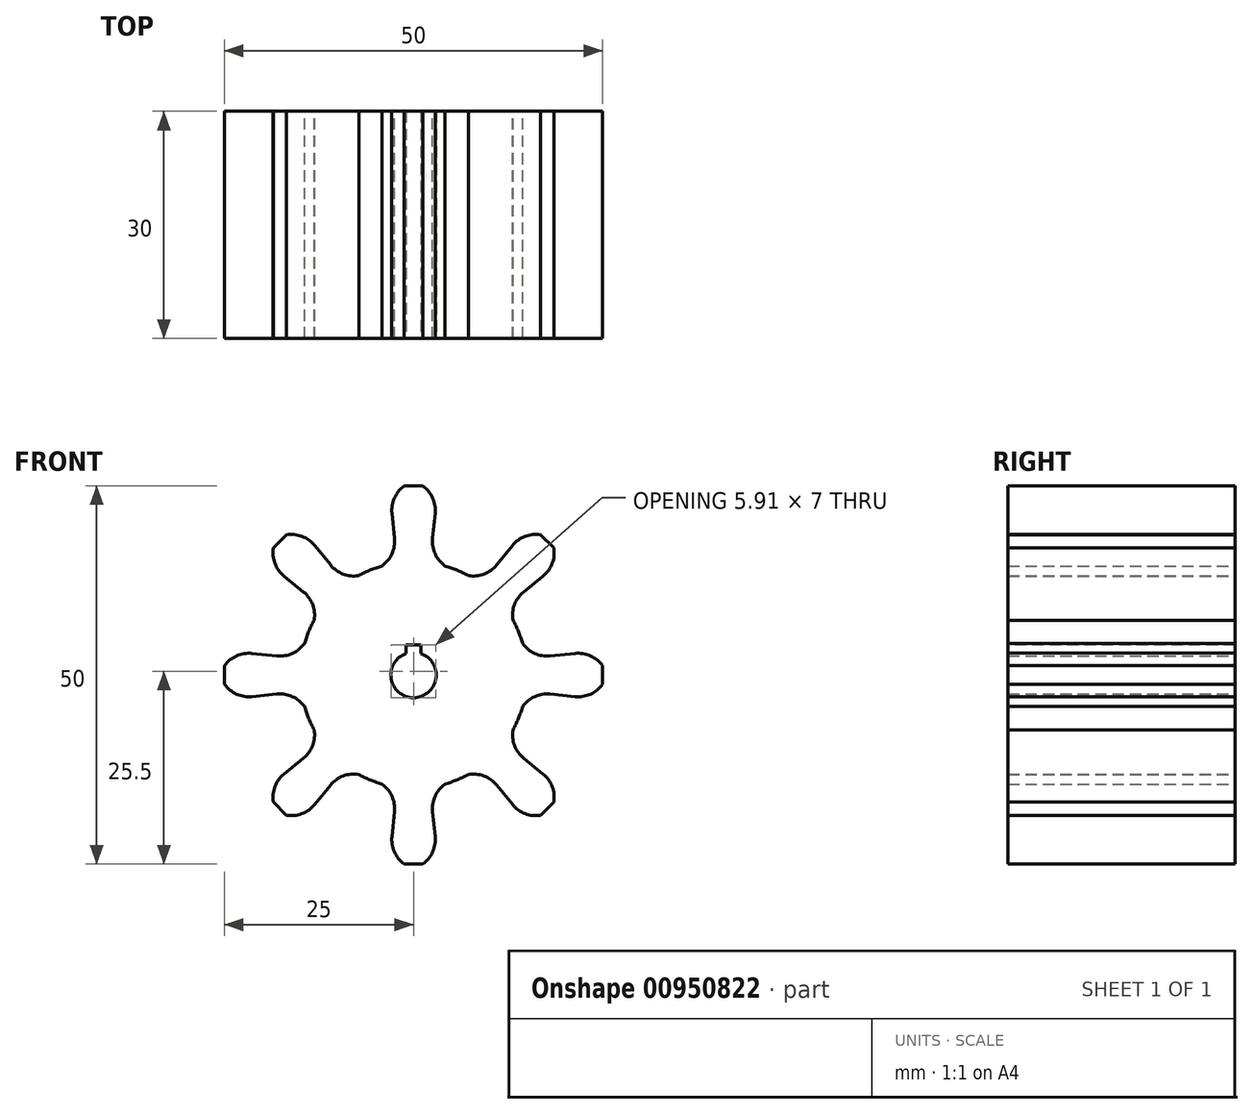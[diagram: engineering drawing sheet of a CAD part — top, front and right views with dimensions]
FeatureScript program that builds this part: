
annotation { "Feature Type Name" : "Feature", "Feature Type Description" : "" }
export const myFeature = defineFeature(function(context is Context, id is Id, definition is map)
    precondition{}
    {
        {
            var Q0;
            Q0=qCreatedBy(makeId("Front.planeOp"),FACE);
            var sketch = newSketch(context, id + "F0", { "sketchPlane" : qUnion([Q0])});
            skArc(sketch, "E0", {"start": v(-13.14, 7.24) * mm, "mid": v(-13.86, 5.74) * mm, "end": v(-14.4, 4.17) * mm});
            skArc(sketch, "E1", {"start": v(-4.17, 14.4) * mm, "mid": v(-2.86, 16.01) * mm, "end": v(-2.53, 18.06) * mm});
            skLineSegment(sketch, "E2", {"start": v(-2.53, 18.06) * mm, "end": v(-2.86, 21.35) * mm});
            skLineSegment(sketch, "E3", {"start": v(-1.22, 25) * mm, "end": v(1.22, 25) * mm});
            skArc(sketch, "E4", {"start": v(-1.22, 25) * mm, "mid": v(-2.53, 23.4) * mm, "end": v(-2.86, 21.35) * mm});
            skArc(sketch, "E5.MirrorCS", {"start": v(1.22, 25) * mm, "mid": v(2.53, 23.4) * mm, "end": v(2.86, 21.35) * mm});
            skLineSegment(sketch, "E6.MirrorCS", {"start": v(2.53, 18.06) * mm, "end": v(2.86, 21.35) * mm});
            skArc(sketch, "E7.MirrorCS", {"start": v(4.17, 14.4) * mm, "mid": v(2.86, 16.01) * mm, "end": v(2.53, 18.06) * mm});
            skLineSegment(sketch, "E8.1.0", {"start": v(-18.54, 16.81) * mm, "end": v(-16.81, 18.54) * mm});
            skArc(sketch, "E8.1.1", {"start": v(-18.54, 16.81) * mm, "mid": v(-18.33, 14.75) * mm, "end": v(-17.12, 13.07) * mm});
            skLineSegment(sketch, "E8.1.2", {"start": v(-14.56, 10.98) * mm, "end": v(-17.12, 13.07) * mm});
            skArc(sketch, "E8.1.3", {"start": v(-13.14, 7.24) * mm, "mid": v(-13.34, 9.3) * mm, "end": v(-14.56, 10.98) * mm});
            skArc(sketch, "E8.1.4", {"start": v(-7.24, 13.14) * mm, "mid": v(-9.3, 13.34) * mm, "end": v(-10.98, 14.56) * mm});
            skLineSegment(sketch, "E8.1.5", {"start": v(-10.98, 14.56) * mm, "end": v(-13.07, 17.12) * mm});
            skArc(sketch, "E8.1.6", {"start": v(-16.81, 18.54) * mm, "mid": v(-14.75, 18.33) * mm, "end": v(-13.07, 17.12) * mm});
            skLineSegment(sketch, "E8.2.0", {"start": v(-25, -1.22) * mm, "end": v(-25, 1.22) * mm});
            skArc(sketch, "E8.2.1", {"start": v(-25, -1.22) * mm, "mid": v(-23.4, -2.53) * mm, "end": v(-21.35, -2.86) * mm});
            skLineSegment(sketch, "E8.2.2", {"start": v(-18.06, -2.53) * mm, "end": v(-21.35, -2.86) * mm});
            skArc(sketch, "E8.2.3", {"start": v(-14.4, -4.17) * mm, "mid": v(-16.01, -2.86) * mm, "end": v(-18.06, -2.53) * mm});
            skArc(sketch, "E8.2.4", {"start": v(-14.4, 4.17) * mm, "mid": v(-16.01, 2.86) * mm, "end": v(-18.06, 2.53) * mm});
            skLineSegment(sketch, "E8.2.5", {"start": v(-18.06, 2.53) * mm, "end": v(-21.35, 2.86) * mm});
            skArc(sketch, "E8.2.6", {"start": v(-25, 1.22) * mm, "mid": v(-23.4, 2.53) * mm, "end": v(-21.35, 2.86) * mm});
            skLineSegment(sketch, "E8.3.0", {"start": v(-16.81, -18.54) * mm, "end": v(-18.54, -16.81) * mm});
            skArc(sketch, "E8.3.1", {"start": v(-16.81, -18.54) * mm, "mid": v(-14.75, -18.33) * mm, "end": v(-13.07, -17.12) * mm});
            skLineSegment(sketch, "E8.3.2", {"start": v(-10.98, -14.56) * mm, "end": v(-13.07, -17.12) * mm});
            skArc(sketch, "E8.3.3", {"start": v(-7.24, -13.14) * mm, "mid": v(-9.3, -13.34) * mm, "end": v(-10.98, -14.56) * mm});
            skArc(sketch, "E8.3.4", {"start": v(-13.14, -7.24) * mm, "mid": v(-13.34, -9.3) * mm, "end": v(-14.56, -10.98) * mm});
            skLineSegment(sketch, "E8.3.5", {"start": v(-14.56, -10.98) * mm, "end": v(-17.12, -13.07) * mm});
            skArc(sketch, "E8.3.6", {"start": v(-18.54, -16.81) * mm, "mid": v(-18.33, -14.75) * mm, "end": v(-17.12, -13.07) * mm});
            skLineSegment(sketch, "E8.4.0", {"start": v(1.22, -25) * mm, "end": v(-1.22, -25) * mm});
            skArc(sketch, "E8.4.1", {"start": v(1.22, -25) * mm, "mid": v(2.53, -23.4) * mm, "end": v(2.86, -21.35) * mm});
            skLineSegment(sketch, "E8.4.2", {"start": v(2.53, -18.06) * mm, "end": v(2.86, -21.35) * mm});
            skArc(sketch, "E8.4.3", {"start": v(4.17, -14.4) * mm, "mid": v(2.86, -16.01) * mm, "end": v(2.53, -18.06) * mm});
            skArc(sketch, "E8.4.4", {"start": v(-4.17, -14.4) * mm, "mid": v(-2.86, -16.01) * mm, "end": v(-2.53, -18.06) * mm});
            skLineSegment(sketch, "E8.4.5", {"start": v(-2.53, -18.06) * mm, "end": v(-2.86, -21.35) * mm});
            skArc(sketch, "E8.4.6", {"start": v(-1.22, -25) * mm, "mid": v(-2.53, -23.4) * mm, "end": v(-2.86, -21.35) * mm});
            skLineSegment(sketch, "E8.5.0", {"start": v(18.54, -16.81) * mm, "end": v(16.81, -18.54) * mm});
            skArc(sketch, "E8.5.1", {"start": v(18.54, -16.81) * mm, "mid": v(18.33, -14.75) * mm, "end": v(17.12, -13.07) * mm});
            skLineSegment(sketch, "E8.5.2", {"start": v(14.56, -10.98) * mm, "end": v(17.12, -13.07) * mm});
            skArc(sketch, "E8.5.3", {"start": v(13.14, -7.24) * mm, "mid": v(13.34, -9.3) * mm, "end": v(14.56, -10.98) * mm});
            skArc(sketch, "E8.5.4", {"start": v(7.24, -13.14) * mm, "mid": v(9.3, -13.34) * mm, "end": v(10.98, -14.56) * mm});
            skLineSegment(sketch, "E8.5.5", {"start": v(10.98, -14.56) * mm, "end": v(13.07, -17.12) * mm});
            skArc(sketch, "E8.5.6", {"start": v(16.81, -18.54) * mm, "mid": v(14.75, -18.33) * mm, "end": v(13.07, -17.12) * mm});
            skLineSegment(sketch, "E8.6.0", {"start": v(25, 1.22) * mm, "end": v(25, -1.22) * mm});
            skArc(sketch, "E8.6.1", {"start": v(25, 1.22) * mm, "mid": v(23.4, 2.53) * mm, "end": v(21.35, 2.86) * mm});
            skLineSegment(sketch, "E8.6.2", {"start": v(18.06, 2.53) * mm, "end": v(21.35, 2.86) * mm});
            skArc(sketch, "E8.6.3", {"start": v(14.4, 4.17) * mm, "mid": v(16.01, 2.86) * mm, "end": v(18.06, 2.53) * mm});
            skArc(sketch, "E8.6.4", {"start": v(14.4, -4.17) * mm, "mid": v(16.01, -2.86) * mm, "end": v(18.06, -2.53) * mm});
            skLineSegment(sketch, "E8.6.5", {"start": v(18.06, -2.53) * mm, "end": v(21.35, -2.86) * mm});
            skArc(sketch, "E8.6.6", {"start": v(25, -1.22) * mm, "mid": v(23.4, -2.53) * mm, "end": v(21.35, -2.86) * mm});
            skLineSegment(sketch, "E8.7.0", {"start": v(16.81, 18.54) * mm, "end": v(18.54, 16.81) * mm});
            skArc(sketch, "E8.7.1", {"start": v(16.81, 18.54) * mm, "mid": v(14.75, 18.33) * mm, "end": v(13.07, 17.12) * mm});
            skLineSegment(sketch, "E8.7.2", {"start": v(10.98, 14.56) * mm, "end": v(13.07, 17.12) * mm});
            skArc(sketch, "E8.7.3", {"start": v(7.24, 13.14) * mm, "mid": v(9.3, 13.34) * mm, "end": v(10.98, 14.56) * mm});
            skArc(sketch, "E8.7.4", {"start": v(13.14, 7.24) * mm, "mid": v(13.34, 9.3) * mm, "end": v(14.56, 10.98) * mm});
            skLineSegment(sketch, "E8.7.5", {"start": v(14.56, 10.98) * mm, "end": v(17.12, 13.07) * mm});
            skArc(sketch, "E8.7.6", {"start": v(18.54, 16.81) * mm, "mid": v(18.33, 14.75) * mm, "end": v(17.12, 13.07) * mm});
            skArc(sketch, "E9.trimOffspring", {"start": v(-4.17, 14.4) * mm, "mid": v(-5.74, 13.86) * mm, "end": v(-7.24, 13.14) * mm});
            skArc(sketch, "E10.trimOffspring", {"start": v(7.24, 13.14) * mm, "mid": v(5.74, 13.86) * mm, "end": v(4.17, 14.4) * mm});
            skArc(sketch, "E11.trimOffspring", {"start": v(14.4, 4.17) * mm, "mid": v(13.86, 5.74) * mm, "end": v(13.14, 7.24) * mm});
            skArc(sketch, "E12.trimOffspring", {"start": v(13.14, -7.24) * mm, "mid": v(13.86, -5.74) * mm, "end": v(14.4, -4.17) * mm});
            skArc(sketch, "E13.trimOffspring", {"start": v(4.17, -14.4) * mm, "mid": v(5.74, -13.86) * mm, "end": v(7.24, -13.14) * mm});
            skArc(sketch, "E14.trimOffspring", {"start": v(-7.24, -13.14) * mm, "mid": v(-5.74, -13.86) * mm, "end": v(-4.17, -14.4) * mm});
            skArc(sketch, "E15.trimOffspring", {"start": v(-14.4, -4.17) * mm, "mid": v(-13.86, -5.74) * mm, "end": v(-13.14, -7.24) * mm});
            skSolve(sketch);
        }
        {
            var Q0;
            Q0=qSketchRegion(id+"F0",true);
            extrude(context, id + "F1", {"entities" : qUnion([Q0]), "depth" : 30 * mm, "offsetDistance" : 25 * mm});
        }
        {
            var Q0;
            Q0=makeQuery(id+"F1.opExtrude","CAP_FACE",FACE,{"disambiguationData":[OSD([sQuery(id+"F0.wireOp",EDGE,"E0"),sQuery(id+"F0.wireOp",EDGE,"E1"),sQuery(id+"F0.wireOp",EDGE,"E2"),sQuery(id+"F0.wireOp",EDGE,"E3"),sQuery(id+"F0.wireOp",EDGE,"E4"),sQuery(id+"F0.wireOp",EDGE,"E5.MirrorCS"),sQuery(id+"F0.wireOp",EDGE,"E6.MirrorCS"),sQuery(id+"F0.wireOp",EDGE,"E7.MirrorCS"),sQuery(id+"F0.wireOp",EDGE,"E8.1.0"),sQuery(id+"F0.wireOp",EDGE,"E8.1.1"),sQuery(id+"F0.wireOp",EDGE,"E8.1.2"),sQuery(id+"F0.wireOp",EDGE,"E8.1.3"),sQuery(id+"F0.wireOp",EDGE,"E8.1.4"),sQuery(id+"F0.wireOp",EDGE,"E8.1.5"),sQuery(id+"F0.wireOp",EDGE,"E8.1.6"),sQuery(id+"F0.wireOp",EDGE,"E8.2.0"),sQuery(id+"F0.wireOp",EDGE,"E8.2.1"),sQuery(id+"F0.wireOp",EDGE,"E8.2.2"),sQuery(id+"F0.wireOp",EDGE,"E8.2.3"),sQuery(id+"F0.wireOp",EDGE,"E8.2.4"),sQuery(id+"F0.wireOp",EDGE,"E8.2.5"),sQuery(id+"F0.wireOp",EDGE,"E8.2.6"),sQuery(id+"F0.wireOp",EDGE,"E8.3.0"),sQuery(id+"F0.wireOp",EDGE,"E8.3.1"),sQuery(id+"F0.wireOp",EDGE,"E8.3.2"),sQuery(id+"F0.wireOp",EDGE,"E8.3.3"),sQuery(id+"F0.wireOp",EDGE,"E8.3.4"),sQuery(id+"F0.wireOp",EDGE,"E8.3.5"),sQuery(id+"F0.wireOp",EDGE,"E8.3.6"),sQuery(id+"F0.wireOp",EDGE,"E8.4.0"),sQuery(id+"F0.wireOp",EDGE,"E8.4.1"),sQuery(id+"F0.wireOp",EDGE,"E8.4.2"),sQuery(id+"F0.wireOp",EDGE,"E8.4.3"),sQuery(id+"F0.wireOp",EDGE,"E8.4.4"),sQuery(id+"F0.wireOp",EDGE,"E8.4.5"),sQuery(id+"F0.wireOp",EDGE,"E8.4.6"),sQuery(id+"F0.wireOp",EDGE,"E8.5.0"),sQuery(id+"F0.wireOp",EDGE,"E8.5.1"),sQuery(id+"F0.wireOp",EDGE,"E8.5.2"),sQuery(id+"F0.wireOp",EDGE,"E8.5.3"),sQuery(id+"F0.wireOp",EDGE,"E8.5.4"),sQuery(id+"F0.wireOp",EDGE,"E8.5.5"),sQuery(id+"F0.wireOp",EDGE,"E8.5.6"),sQuery(id+"F0.wireOp",EDGE,"E8.6.0"),sQuery(id+"F0.wireOp",EDGE,"E8.6.1"),sQuery(id+"F0.wireOp",EDGE,"E8.6.2"),sQuery(id+"F0.wireOp",EDGE,"E8.6.3"),sQuery(id+"F0.wireOp",EDGE,"E8.6.4"),sQuery(id+"F0.wireOp",EDGE,"E8.6.5"),sQuery(id+"F0.wireOp",EDGE,"E8.6.6"),sQuery(id+"F0.wireOp",EDGE,"E8.7.0"),sQuery(id+"F0.wireOp",EDGE,"E8.7.1"),sQuery(id+"F0.wireOp",EDGE,"E8.7.2"),sQuery(id+"F0.wireOp",EDGE,"E8.7.3"),sQuery(id+"F0.wireOp",EDGE,"E8.7.4"),sQuery(id+"F0.wireOp",EDGE,"E8.7.5"),sQuery(id+"F0.wireOp",EDGE,"E8.7.6"),sQuery(id+"F0.wireOp",EDGE,"E9.trimOffspring"),sQuery(id+"F0.wireOp",EDGE,"E10.trimOffspring"),sQuery(id+"F0.wireOp",EDGE,"E11.trimOffspring"),sQuery(id+"F0.wireOp",EDGE,"E12.trimOffspring"),sQuery(id+"F0.wireOp",EDGE,"E13.trimOffspring"),sQuery(id+"F0.wireOp",EDGE,"E14.trimOffspring"),sQuery(id+"F0.wireOp",EDGE,"E15.trimOffspring")])],"isStart":false});
            var sketch = newSketch(context, id + "F2", { "sketchPlane" : qUnion([Q0])});
            skPoint(sketch, "E16.0.midPoint", {"position": v(2.04, 3.54) * mm});
            skArc(sketch, "E17", {"start": v(-1, 2.83) * mm, "mid": v(0, -3) * mm, "end": v(1, 2.83) * mm});
            skLineSegment(sketch, "E18", {"start": v(-1, 2.83) * mm, "end": v(-1, 4) * mm});
            skLineSegment(sketch, "E19", {"start": v(-1, 4) * mm, "end": v(1, 4) * mm});
            skLineSegment(sketch, "E20", {"start": v(1, 4) * mm, "end": v(1, 2.83) * mm});
            skSolve(sketch);
        }
        {
            var Q0;
            Q0=qSketchRegion(id+"F2",true);
            extrude(context, id + "F3", {"entities" : qUnion([Q0]), "operationType" : NewBodyOperationType.REMOVE, "endBound" : BoundingType.THROUGH_ALL, "oppositeDirection" : true, "depth" : 25 * mm, "offsetDistance" : 25 * mm});
        }
    });
